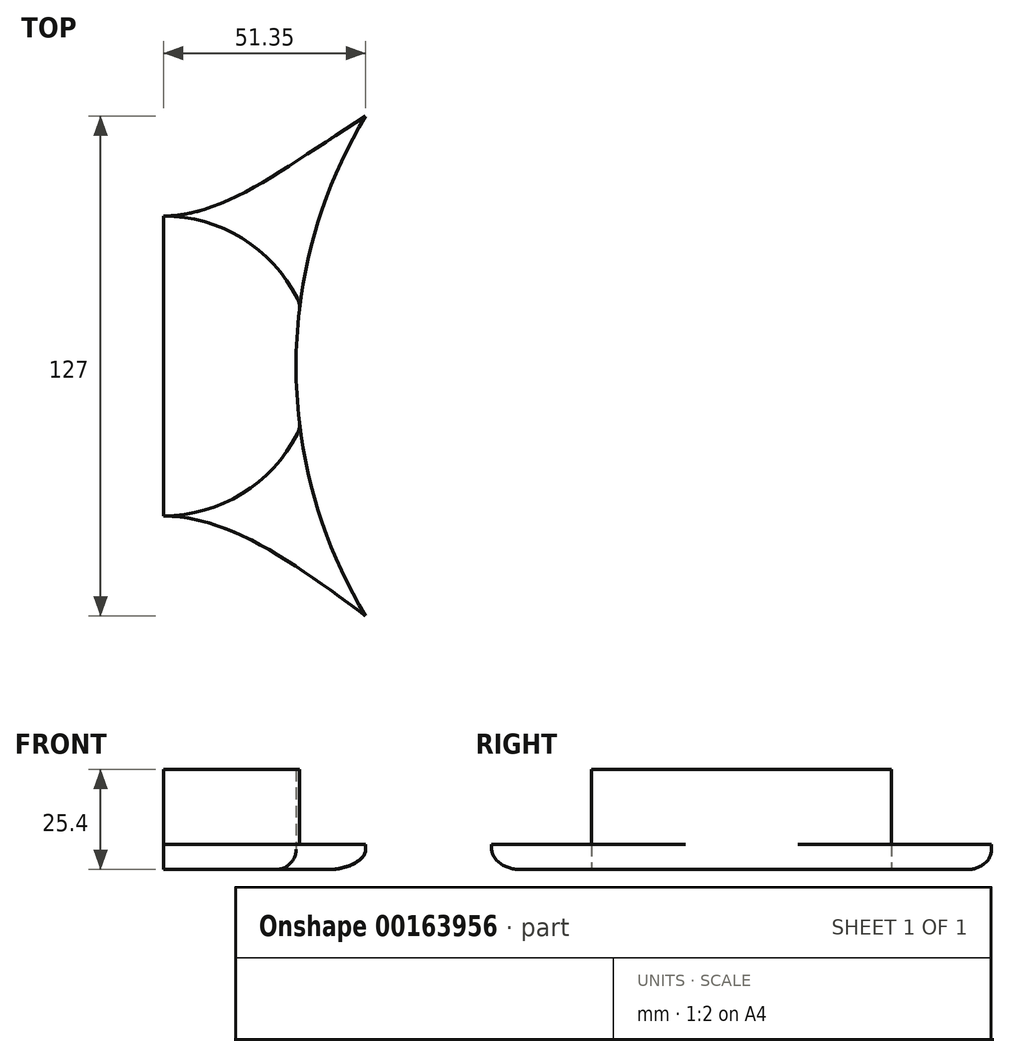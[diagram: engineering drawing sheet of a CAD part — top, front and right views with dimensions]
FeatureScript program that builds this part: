
annotation { "Feature Type Name" : "Feature", "Feature Type Description" : "" }
export const myFeature = defineFeature(function(context is Context, id is Id, definition is map)
    precondition{}
    {
        {
            var Q0;
            Q0=qCreatedBy(makeId("Top.planeOp"),FACE);
            var sketch = newSketch(context, id + "F0", { "sketchPlane" : qUnion([Q0])});
            skCircle(sketch, "E0", {"center": v(0, 0) * mm, "radius": 38.1 * mm});
            skLineSegment(sketch, "E1", {"start": v(0, 0) * mm, "end": v(0, 63.5) * mm});
            skLineSegment(sketch, "E2", {"start": v(0, 0) * mm, "end": v(0, -63.5) * mm});
            skArc(sketch, "E3", {"start": v(51.35, 63.5) * mm, "mid": v(33.69, 0) * mm, "end": v(51.35, -63.5) * mm});
            skArc(sketch, "E4.MirrorCS", {"start": v(-51.35, 63.5) * mm, "mid": v(-33.69, 0) * mm, "end": v(-51.35, -63.5) * mm});
            skFitSpline(sketch, "E5", {"points": [v(-51.35, -63.5) * mm, v(0, -38.1) * mm, v(51.35, -63.5) * mm], "startDerivative": vector(102.7, 76.2) * mm, "endDerivative": vector(102.7, -76.2) * mm});
            skFitSpline(sketch, "E6", {"points": [v(-51.35, 63.5) * mm, v(0, 38.1) * mm, v(51.35, 63.5) * mm], "startDerivative": vector(119.72, -76.2) * mm, "endDerivative": vector(119.72, 76.2) * mm});
            skSolve(sketch);
        }
        {
            var Q0;
            {var subQ3=sQuery(id+"F0.wireOp",EDGE,"E0");var subQ6=sQuery(id+"F0.wireOp",EDGE,"E4.MirrorCS");var subQ8=makeQuery(id+"F0.imprint","INTERSECT",VERTEX,{"disambiguationData":[OD(0.0)],"derivedFrom":[subQ3,subQ6]});Q0=makeQuery(id+"F0.imprint","IMPRINT",FACE,{"disambiguationData":[TD([[makeQuery(id+"F0.imprint","IMPRINT",EDGE,{"disambiguationData":[TD([[subQ8,-1.0]])],"derivedFrom":subQ6}),1.0]])]});}
            var Q1;
            {var subQ3=sQuery(id+"F0.wireOp",EDGE,"E0");var subQ6=sQuery(id+"F0.wireOp",EDGE,"E3");var subQ8=makeQuery(id+"F0.imprint","INTERSECT",VERTEX,{"disambiguationData":[OD(0.0)],"derivedFrom":[subQ3,subQ6]});Q1=makeQuery(id+"F0.imprint","IMPRINT",FACE,{"disambiguationData":[TD([[makeQuery(id+"F0.imprint","IMPRINT",EDGE,{"disambiguationData":[TD([[subQ8,-1.0]])],"derivedFrom":subQ6}),-1.0]])]});}
            extrude(context, id + "F1", {"entities" : qUnion([Q0, Q1]), "depth" : 25.4 * mm});
        }
        {
            var Q0;
            {var subQ0=sQuery(id+"F0.wireOp",EDGE,"E4.MirrorCS");var subQ3=sQuery(id+"F0.wireOp",EDGE,"E5");var subQ5=makeQuery(id+"F0.imprint","INTERSECT",VERTEX,{"derivedFrom":[subQ0,subQ3]});Q0=makeQuery(id+"F0.imprint","IMPRINT",FACE,{"disambiguationData":[TD([[makeQuery(id+"F0.imprint","IMPRINT",EDGE,{"disambiguationData":[TD([[subQ5,1.0]])],"derivedFrom":subQ0}),1.0]])]});}
            var Q1;
            {var subQ0=sQuery(id+"F0.wireOp",EDGE,"E3");var subQ3=sQuery(id+"F0.wireOp",EDGE,"E5");var subQ5=makeQuery(id+"F0.imprint","INTERSECT",VERTEX,{"derivedFrom":[subQ0,subQ3]});Q1=makeQuery(id+"F0.imprint","IMPRINT",FACE,{"disambiguationData":[TD([[makeQuery(id+"F0.imprint","IMPRINT",EDGE,{"disambiguationData":[TD([[subQ5,1.0]])],"derivedFrom":subQ0}),-1.0]])]});}
            var Q2;
            {var subQ0=sQuery(id+"F0.wireOp",EDGE,"E3");var subQ3=sQuery(id+"F0.wireOp",EDGE,"E6");var subQ5=makeQuery(id+"F0.imprint","INTERSECT",VERTEX,{"derivedFrom":[subQ0,subQ3]});Q2=makeQuery(id+"F0.imprint","IMPRINT",FACE,{"disambiguationData":[TD([[makeQuery(id+"F0.imprint","IMPRINT",EDGE,{"disambiguationData":[TD([[subQ5,-1.0]])],"derivedFrom":subQ0}),-1.0]])]});}
            var Q3;
            {var subQ0=sQuery(id+"F0.wireOp",EDGE,"E4.MirrorCS");var subQ3=sQuery(id+"F0.wireOp",EDGE,"E6");var subQ5=makeQuery(id+"F0.imprint","INTERSECT",VERTEX,{"derivedFrom":[subQ0,subQ3]});Q3=makeQuery(id+"F0.imprint","IMPRINT",FACE,{"disambiguationData":[TD([[makeQuery(id+"F0.imprint","IMPRINT",EDGE,{"disambiguationData":[TD([[subQ5,-1.0]])],"derivedFrom":subQ0}),1.0]])]});}
            extrude(context, id + "F2", {"entities" : qUnion([Q0, Q1, Q2, Q3]), "operationType" : NewBodyOperationType.ADD, "depth" : 6.35 * mm});
        }
        {
            var Q0;
            {var subQ0=sQuery(id+"F0.wireOp",EDGE,"E6");Q0=makeQuery(id+"F2.boolean.opBoolean","MERGE",EDGE,{"derivedFrom":[makeQuery(id+"F2.opExtrude","CAP_EDGE",EDGE,{"disambiguationData":[OSD([subQ0]),TDD([makeQuery(id+"F0.imprint","IMPRINT",EDGE,{"disambiguationData":[TD([[makeQuery(id+"F0.imprint","INTERSECT",VERTEX,{"derivedFrom":[sQuery(id+"F0.wireOp",EDGE,"E4.MirrorCS"),subQ0]}),-1.0]])],"derivedFrom":subQ0})])],"isStart":true}),makeQuery(id+"F2.opExtrude","CAP_EDGE",EDGE,{"disambiguationData":[OSD([subQ0]),TDD([makeQuery(id+"F0.imprint","IMPRINT",EDGE,{"disambiguationData":[TD([[makeQuery(id+"F0.imprint","INTERSECT",VERTEX,{"derivedFrom":[sQuery(id+"F0.wireOp",EDGE,"E3"),subQ0]}),1.0]])],"derivedFrom":subQ0})])],"isStart":true})]});}
            var Q1;
            {var subQ0=sQuery(id+"F0.wireOp",EDGE,"E5");Q1=makeQuery(id+"F2.boolean.opBoolean","MERGE",EDGE,{"derivedFrom":[makeQuery(id+"F2.opExtrude","CAP_EDGE",EDGE,{"disambiguationData":[OSD([subQ0]),TDD([makeQuery(id+"F0.imprint","IMPRINT",EDGE,{"disambiguationData":[TD([[makeQuery(id+"F0.imprint","INTERSECT",VERTEX,{"derivedFrom":[sQuery(id+"F0.wireOp",EDGE,"E4.MirrorCS"),subQ0]}),-1.0]])],"derivedFrom":subQ0})])],"isStart":true}),makeQuery(id+"F2.opExtrude","CAP_EDGE",EDGE,{"disambiguationData":[OSD([subQ0]),TDD([makeQuery(id+"F0.imprint","IMPRINT",EDGE,{"disambiguationData":[TD([[makeQuery(id+"F0.imprint","INTERSECT",VERTEX,{"derivedFrom":[sQuery(id+"F0.wireOp",EDGE,"E3"),subQ0]}),1.0]])],"derivedFrom":subQ0})])],"isStart":true})]});}
            var Q2;
            {var subQ0=sQuery(id+"F0.wireOp",EDGE,"E4.MirrorCS");Q2=makeQuery(id+"F2.boolean.opBoolean","MERGE",EDGE,{"derivedFrom":[makeQuery(id+"F1.opExtrude","CAP_EDGE",EDGE,{"disambiguationData":[OSD([subQ0])],"isStart":true}),makeQuery(id+"F2.opExtrude","CAP_EDGE",EDGE,{"disambiguationData":[OSD([subQ0]),TDD([makeQuery(id+"F0.imprint","IMPRINT",EDGE,{"disambiguationData":[TD([[makeQuery(id+"F0.imprint","INTERSECT",VERTEX,{"derivedFrom":[subQ0,sQuery(id+"F0.wireOp",EDGE,"E6")]}),-1.0]])],"derivedFrom":subQ0})])],"isStart":true}),makeQuery(id+"F2.opExtrude","CAP_EDGE",EDGE,{"disambiguationData":[OSD([subQ0]),TDD([makeQuery(id+"F0.imprint","IMPRINT",EDGE,{"disambiguationData":[TD([[makeQuery(id+"F0.imprint","INTERSECT",VERTEX,{"derivedFrom":[subQ0,sQuery(id+"F0.wireOp",EDGE,"E5")]}),1.0]])],"derivedFrom":subQ0})])],"isStart":true})]});}
            var Q3;
            {var subQ0=sQuery(id+"F0.wireOp",EDGE,"E3");Q3=makeQuery(id+"F2.boolean.opBoolean","MERGE",EDGE,{"derivedFrom":[makeQuery(id+"F1.opExtrude","CAP_EDGE",EDGE,{"disambiguationData":[OSD([subQ0])],"isStart":true}),makeQuery(id+"F2.opExtrude","CAP_EDGE",EDGE,{"disambiguationData":[OSD([subQ0]),TDD([makeQuery(id+"F0.imprint","IMPRINT",EDGE,{"disambiguationData":[TD([[makeQuery(id+"F0.imprint","INTERSECT",VERTEX,{"derivedFrom":[subQ0,sQuery(id+"F0.wireOp",EDGE,"E6")]}),-1.0]])],"derivedFrom":subQ0})])],"isStart":true}),makeQuery(id+"F2.opExtrude","CAP_EDGE",EDGE,{"disambiguationData":[OSD([subQ0]),TDD([makeQuery(id+"F0.imprint","IMPRINT",EDGE,{"disambiguationData":[TD([[makeQuery(id+"F0.imprint","INTERSECT",VERTEX,{"derivedFrom":[subQ0,sQuery(id+"F0.wireOp",EDGE,"E5")]}),1.0]])],"derivedFrom":subQ0})])],"isStart":true})]});}
            var Q4;
            {var subQ0=sQuery(id+"F0.wireOp",EDGE,"E3");var subQ1=sQuery(id+"F0.wireOp",EDGE,"E0");Q4=makeQuery(id+"F1.opExtrude","SWEPT_EDGE",EDGE,{"disambiguationData":[OSD([subQ1,subQ0]),TDD([makeQuery(id+"F0.imprint","INTERSECT",VERTEX,{"disambiguationData":[OD(0.0)],"derivedFrom":[subQ1,subQ0]})])]});}
            var Q5;
            {var subQ0=sQuery(id+"F0.wireOp",EDGE,"E3");var subQ1=sQuery(id+"F0.wireOp",EDGE,"E0");Q5=makeQuery(id+"F1.opExtrude","SWEPT_EDGE",EDGE,{"disambiguationData":[OSD([subQ1,subQ0]),TDD([makeQuery(id+"F0.imprint","INTERSECT",VERTEX,{"disambiguationData":[OD(1.0)],"derivedFrom":[subQ1,subQ0]})])]});}
            var Q6;
            {var subQ0=sQuery(id+"F0.wireOp",EDGE,"E4.MirrorCS");var subQ1=sQuery(id+"F0.wireOp",EDGE,"E0");Q6=makeQuery(id+"F1.opExtrude","SWEPT_EDGE",EDGE,{"disambiguationData":[OSD([subQ1,subQ0]),TDD([makeQuery(id+"F0.imprint","INTERSECT",VERTEX,{"disambiguationData":[OD(0.0)],"derivedFrom":[subQ1,subQ0]})])]});}
            var Q7;
            {var subQ0=sQuery(id+"F0.wireOp",EDGE,"E4.MirrorCS");var subQ1=sQuery(id+"F0.wireOp",EDGE,"E0");Q7=makeQuery(id+"F1.opExtrude","SWEPT_EDGE",EDGE,{"disambiguationData":[OSD([subQ1,subQ0]),TDD([makeQuery(id+"F0.imprint","INTERSECT",VERTEX,{"disambiguationData":[OD(1.0)],"derivedFrom":[subQ1,subQ0]})])]});}
            fillet(context, id + "F3", {"entities" : qUnion([Q0, Q1, Q2, Q3, Q4, Q5, Q6, Q7]), "radius" : 5.08 * mm, "tangentPropagation" : true, "allowEdgeOverflow" : false});
        }
    });
